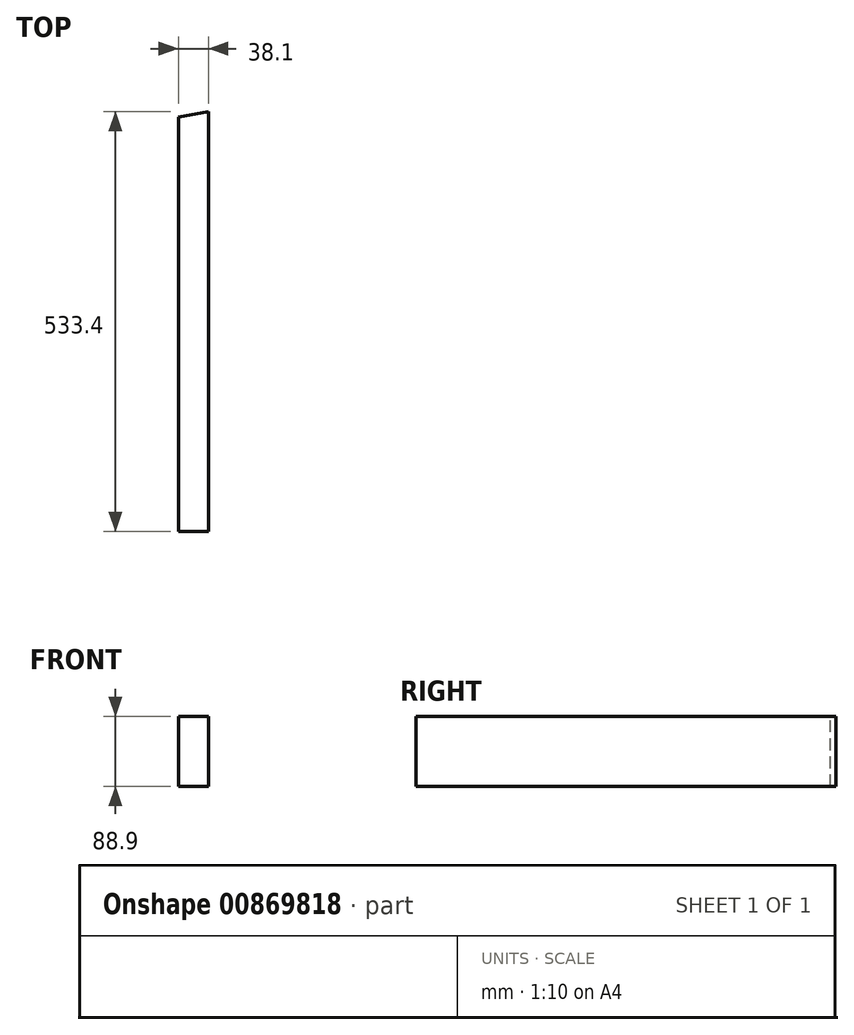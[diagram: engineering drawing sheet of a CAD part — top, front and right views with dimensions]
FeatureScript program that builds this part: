
annotation { "Feature Type Name" : "Feature", "Feature Type Description" : "" }
export const myFeature = defineFeature(function(context is Context, id is Id, definition is map)
    precondition{}
    {
        {
            var Q0;
            Q0=qCreatedBy(makeId("Front.planeOp"),FACE);
            var sketch = newSketch(context, id + "F0", { "sketchPlane" : qUnion([Q0])});
            skLineSegment(sketch, "E0.bottom", {"start": v(19.05, -44.45) * mm, "end": v(-19.05, -44.45) * mm});
            skLineSegment(sketch, "E0.top", {"start": v(19.05, 44.45) * mm, "end": v(-19.05, 44.45) * mm});
            skLineSegment(sketch, "E0.left", {"start": v(19.05, -44.45) * mm, "end": v(19.05, 44.45) * mm});
            skLineSegment(sketch, "E0.right", {"start": v(-19.05, -44.45) * mm, "end": v(-19.05, 44.45) * mm});
            skPoint(sketch, "E0.middle", {"position": v(0, 0) * mm});
            skSolve(sketch);
        }
        {
            var Q0;
            Q0 = qSketchRegion(id + "F0", true);
            extrude(context, id + "F1", {"entities" : qUnion([Q0]), "oppositeDirection" : true, "depth" : 533.4 * mm, "offsetDistance" : 25.4 * mm});
        }
        {
            var Q0;
            Q0=makeQuery(id+"F1.opExtrude","SWEPT_FACE",FACE,{"disambiguationData":[OSD([sQuery(id+"F0.wireOp",EDGE,"E0.top")])]});
            var sketch = newSketch(context, id + "F2", { "sketchPlane" : qUnion([Q0])});
            skLineSegment(sketch, "E1", {"start": v(19.05, 533.4) * mm, "end": v(-19.05, 526.68) * mm});
            skLineSegment(sketch, "E2", {"start": v(-19.05, 526.68) * mm, "end": v(-19.05, 533.4) * mm});
            skLineSegment(sketch, "E3", {"start": v(-19.05, 533.4) * mm, "end": v(19.05, 533.4) * mm});
            skSolve(sketch);
        }
        {
            var Q0;
            Q0 = qSketchRegion(id + "F2", true);
            extrude(context, id + "F3", {"entities" : qUnion([Q0]), "operationType" : NewBodyOperationType.REMOVE, "endBound" : BoundingType.THROUGH_ALL, "oppositeDirection" : true, "depth" : 25.4 * mm, "offsetDistance" : 25.4 * mm});
        }
    });
